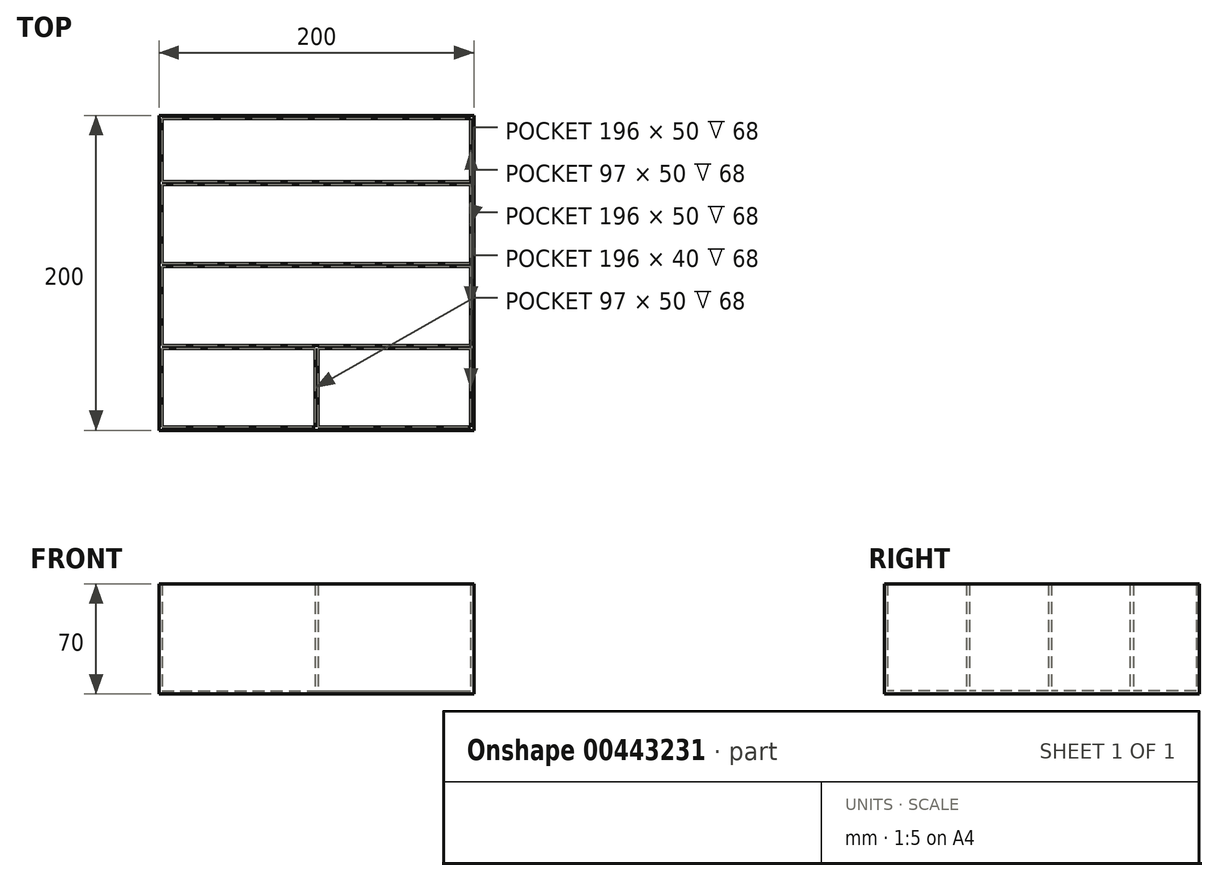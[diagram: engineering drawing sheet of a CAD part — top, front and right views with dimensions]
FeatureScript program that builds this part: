
annotation { "Feature Type Name" : "Feature", "Feature Type Description" : "" }
export const myFeature = defineFeature(function(context is Context, id is Id, definition is map)
    precondition{}
    {
        {
            var Q0;
            Q0=qCreatedBy(makeId("Top.planeOp"),FACE);
            var sketch = newSketch(context, id + "F0", { "sketchPlane" : qUnion([Q0])});
            skLineSegment(sketch, "E0.bottom", {"start": v(-111.65, 97.34) * mm, "end": v(88.35, 97.34) * mm});
            skLineSegment(sketch, "E0.top", {"start": v(-111.65, -102.66) * mm, "end": v(88.35, -102.66) * mm});
            skLineSegment(sketch, "E0.left", {"start": v(-111.65, 97.34) * mm, "end": v(-111.65, -102.66) * mm});
            skLineSegment(sketch, "E0.right", {"start": v(88.35, 97.34) * mm, "end": v(88.35, -102.66) * mm});
            skSolve(sketch);
        }
        {
            var Q0;
            Q0=makeQuery(id+"F0.imprint","IMPRINT",FACE,{"disambiguationData":[TD([[makeQuery(id+"F0.imprint","IMPRINT",EDGE,{"derivedFrom":sQuery(id+"F0.wireOp",EDGE,"E0.bottom")}),-1.0]])]});
            extrude(context, id + "F1", {"entities" : qUnion([Q0]), "depth" : 70 * mm});
        }
        {
            var Q0;
            Q0=makeQuery(id+"F1.opExtrude","CAP_FACE",FACE,{"disambiguationData":[OSD([sQuery(id+"F0.wireOp",EDGE,"E0.bottom"),sQuery(id+"F0.wireOp",EDGE,"E0.top"),sQuery(id+"F0.wireOp",EDGE,"E0.left"),sQuery(id+"F0.wireOp",EDGE,"E0.right")])],"isStart":false});
            shell(context, id + "F2", {"entities" : qUnion([Q0]), "thickness" : 2 * mm});
        }
        {
            var Q0;
            Q0=makeQuery(id+"F2.opShell","OFFSET_FACE",FACE,{"disambiguationData":[OSD([sQuery(id+"F0.wireOp",EDGE,"E0.bottom"),sQuery(id+"F0.wireOp",EDGE,"E0.top"),sQuery(id+"F0.wireOp",EDGE,"E0.left"),sQuery(id+"F0.wireOp",EDGE,"E0.right")])]});
            var sketch = newSketch(context, id + "F3", { "sketchPlane" : qUnion([Q0])});
            skLineSegment(sketch, "E1", {"start": v(-109.65, 55.34) * mm, "end": v(86.35, 55.34) * mm});
            skLineSegment(sketch, "E2", {"start": v(-109.65, 53.34) * mm, "end": v(86.35, 53.34) * mm});
            skLineSegment(sketch, "E3", {"start": v(-109.65, 3.34) * mm, "end": v(86.35, 3.34) * mm});
            skLineSegment(sketch, "E4", {"start": v(-109.65, 1.34) * mm, "end": v(86.35, 1.34) * mm});
            skLineSegment(sketch, "E5", {"start": v(-109.65, -48.66) * mm, "end": v(86.35, -48.66) * mm});
            skLineSegment(sketch, "E6", {"start": v(-109.65, -50.66) * mm, "end": v(86.35, -50.66) * mm});
            skLineSegment(sketch, "E7", {"start": v(-12.65, -50.66) * mm, "end": v(-12.65, -100.66) * mm});
            skLineSegment(sketch, "E8", {"start": v(-10.65, -50.66) * mm, "end": v(-10.65, -100.66) * mm});
            skSolve(sketch);
        }
        {
            var Q0;
            {var subQ0=sQuery(id+"F3.wireOp",EDGE,"E1");Q0=makeQuery(id+"F3.imprint","IMPRINT",FACE,{"disambiguationData":[TD([[makeQuery(id+"F3.imprint","IMPRINT",EDGE,{"derivedFrom":subQ0}),-1.0]])]});}
            var Q1;
            {var subQ0=sQuery(id+"F3.wireOp",EDGE,"E3");Q1=makeQuery(id+"F3.imprint","IMPRINT",FACE,{"disambiguationData":[TD([[makeQuery(id+"F3.imprint","IMPRINT",EDGE,{"derivedFrom":subQ0}),-1.0]])]});}
            var Q2;
            {var subQ9=sQuery(id+"F3.wireOp",EDGE,"E5");Q2=makeQuery(id+"F3.imprint","IMPRINT",FACE,{"disambiguationData":[TD([[makeQuery(id+"F3.imprint","IMPRINT",EDGE,{"derivedFrom":subQ9}),-1.0]])]});}
            var Q3;
            {var subQ0=sQuery(id+"F3.wireOp",EDGE,"E7");Q3=makeQuery(id+"F3.imprint","IMPRINT",FACE,{"disambiguationData":[TD([[makeQuery(id+"F3.imprint","IMPRINT",EDGE,{"derivedFrom":subQ0}),1.0]])]});}
            extrude(context, id + "F4", {"entities" : qUnion([Q0, Q1, Q2, Q3]), "operationType" : NewBodyOperationType.ADD, "depth" : 68 * mm, "offsetDistance" : 25 * mm});
        }
    });
